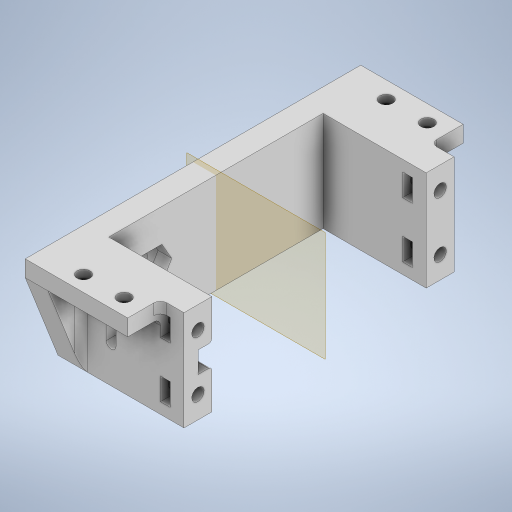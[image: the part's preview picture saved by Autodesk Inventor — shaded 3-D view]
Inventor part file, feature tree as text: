
AUTODESK INVENTOR PART (.ipt)
format: ipt  version: 2024 (Build 280153020, 153B)  size: 425,472 bytes
history: native  units: mm
features: sketch x11, extrude x10, fillet x2, plane x1, mirror x1, hole x1
ambient origin geometry x8: Origin, YZ Plane, XZ Plane, XY Plane, X Axis, Y Axis, Z Axis, Center Point
bodies: Body1 (feature_tree)
feature tree (26):
  extrude  "Extrusion2"  Depth=82.5mm
  extrude  "Extrusion3"  Depth=65.5mm
  extrude  "Extrusion4"  Depth=8.5mm
  extrude  "Extrusion6"  Depth=8.5mm
  extrude  "Extrusion7"  Depth=31.5mm TaperAngle=0.0deg
  extrude  "Extrusion9"  Depth=7.0mm TaperAngle=0.0deg
  extrude  "Extrusion10"  Depth=5.25mm
  fillet  "Fillet1"  Radius=4.2mm
  extrude  "Extrusion12"  TaperAngle=0.0deg  [1 undecoded]
  extrude  "Extrusion13"  Depth=3.25mm
  plane  "Work Plane1"
  mirror  "Mirror1"
  extrude  "Extrusion14"  Depth=3.25mm
  fillet  "Fillet3"  Radius=3.25mm
  hole  "Hole1"  [1 undecoded]
  sketch  "Sketch2"  dims[d0=30.5mm d1=82.5mm]
  sketch  "Sketch4"  dims[d2=30.5mm d3=65.5mm]
  sketch  "Sketch5"  dims[d4=4.25mm d6=8.5mm]
  sketch  "Sketch8"  dims[d7=8.5mm d8=8.5mm]
  sketch  "Sketch9"  dims[d14=3.8mm d15=31.5mm d16=0.0mm]
  sketch  "Sketch10"  dims[d17=23.5mm d18=0.0mm d19=7.0mm d20=0.0mm]
  sketch  "Sketch12"  dims[d25=13.2mm d26=5.25mm d27=4.2mm d28=0.0mm]
  sketch  "Sketch13"  dims[d29=5.75mm d30=0.0mm d31=0.0mm]
  sketch  "Sketch16"  dims[d41=0.0mm d42=0.0mm d44=3.25mm]
  sketch  "Sketch18"  dims[d46=4.2mm d47=3.25mm d48=3.25mm]
  sketch  "Sketch19"  dims[d49=4.2mm d50=10.0mm d51=0.0mm d52=1.0mm d61=4.2mm d62=3.4mm d63=3.0mm d64=6.8mm d65=3.0mm d66=3.4mm d70=73.6mm d71=0.0mm d72=8.1mm d73=0.0mm d76=5.0mm d77=10.0mm d78=0.0mm d80=7.0mm d81=0.0mm d82=2.0mm d83=4.0mm d84=6.0mm d85=9.2mm d86=2.0mm d87=90.0deg d88=8.0mm d89=20.594885mm]
note: 2 required parameter values undecoded (feature->parameter linkage not recoverable at this tier; creation-order binding heuristic only, values carry confidence <= 0.55)
